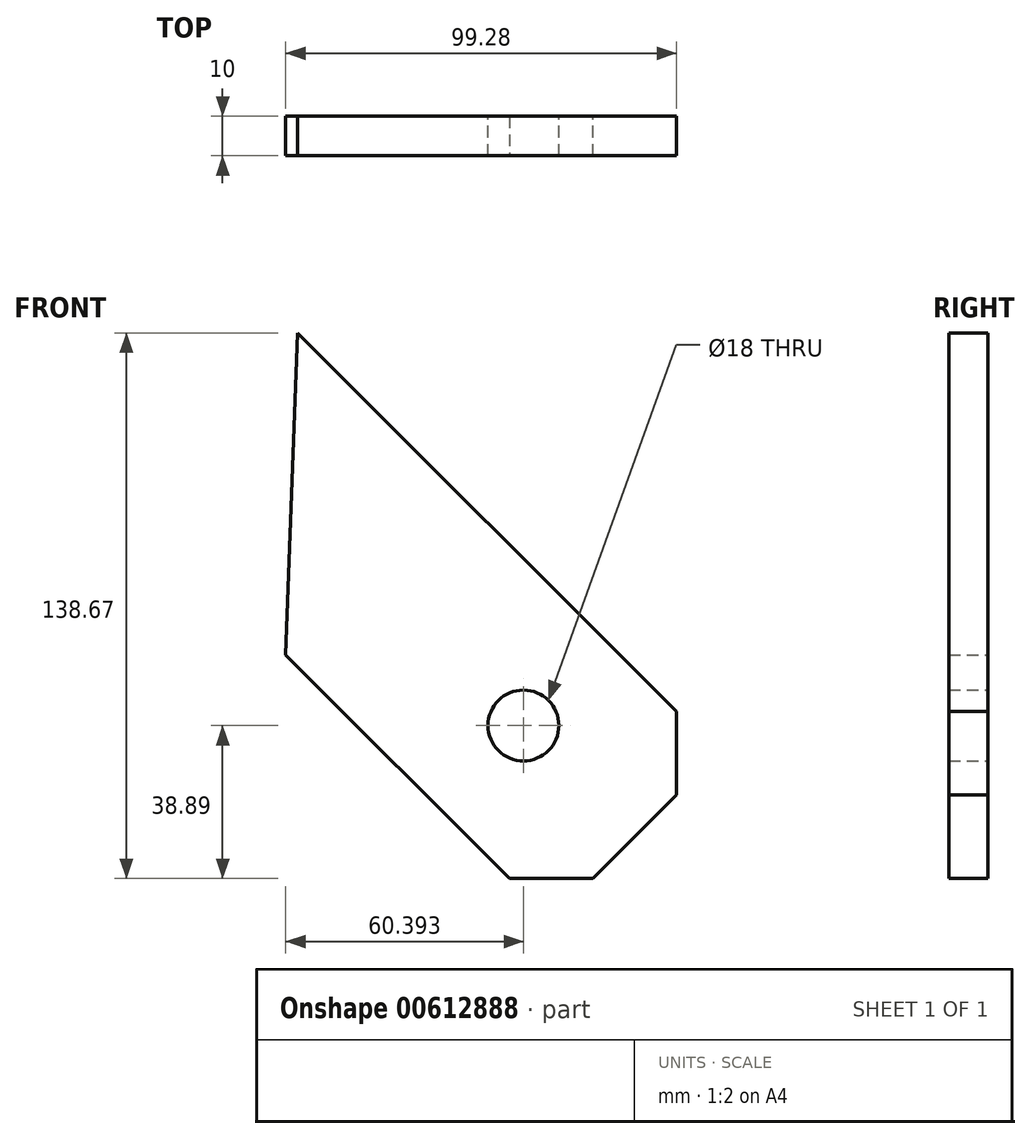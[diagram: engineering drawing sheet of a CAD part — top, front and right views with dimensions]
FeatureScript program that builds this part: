
annotation { "Feature Type Name" : "Feature", "Feature Type Description" : "" }
export const myFeature = defineFeature(function(context is Context, id is Id, definition is map)
    precondition{}
    {
        {
            var Q0;
            Q0=qCreatedBy(makeId("Front.planeOp"),FACE);
            var sketch = newSketch(context, id + "F0", { "sketchPlane" : qUnion([Q0])});
            skCircle(sketch, "E0", {"center": v(57.35, -300) * mm, "radius": 9 * mm});
            skLineSegment(sketch, "E1", {"start": v(78.57, -278.79) * mm, "end": v(0, -200.22) * mm});
            skLineSegment(sketch, "E2", {"start": v(78.57, -278.79) * mm, "end": v(106.85, -307.07) * mm});
            skLineSegment(sketch, "E3", {"start": v(106.85, -307.07) * mm, "end": v(64.42, -349.5) * mm});
            skLineSegment(sketch, "E4", {"start": v(-3.15, -285.02) * mm, "end": v(0, -200.22) * mm});
            skLineSegment(sketch, "E5", {"start": v(64.42, -349.5) * mm, "end": v(-3.04, -282.03) * mm});
            skSolve(sketch);
        }
        {
            var Q0;
            Q0=makeQuery(id+"F0.imprint","IMPRINT",FACE,{"disambiguationData":[TD([[makeQuery(id+"F0.imprint","IMPRINT",EDGE,{"derivedFrom":sQuery(id+"F0.wireOp",EDGE,"E0")}),-1.0]])]});
            extrude(context, id + "F1", {"entities" : qUnion([Q0]), "depth" : 10 * mm, "offsetDistance" : 25 * mm});
        }
        {
            var Q0;
            Q0=makeQuery(id+"F1.opExtrude","SWEPT_EDGE",EDGE,{"disambiguationData":[OSD([sQuery(id+"F0.wireOp",EDGE,"E2"),sQuery(id+"F0.wireOp",EDGE,"E3")])]});
            var Q1;
            Q1=makeQuery(id+"F1.opExtrude","SWEPT_EDGE",EDGE,{"disambiguationData":[OSD([sQuery(id+"F0.wireOp",EDGE,"E3"),sQuery(id+"F0.wireOp",EDGE,"11nyvhHw-jBOW-6WRT-f1eJ-v4boGJ1LN2ox")])]});
            chamfer(context, id + "F2", {"entities" : qUnion([Q0, Q1]), "width" : 15 * mm, "tangentPropagation" : true});
        }
    });
